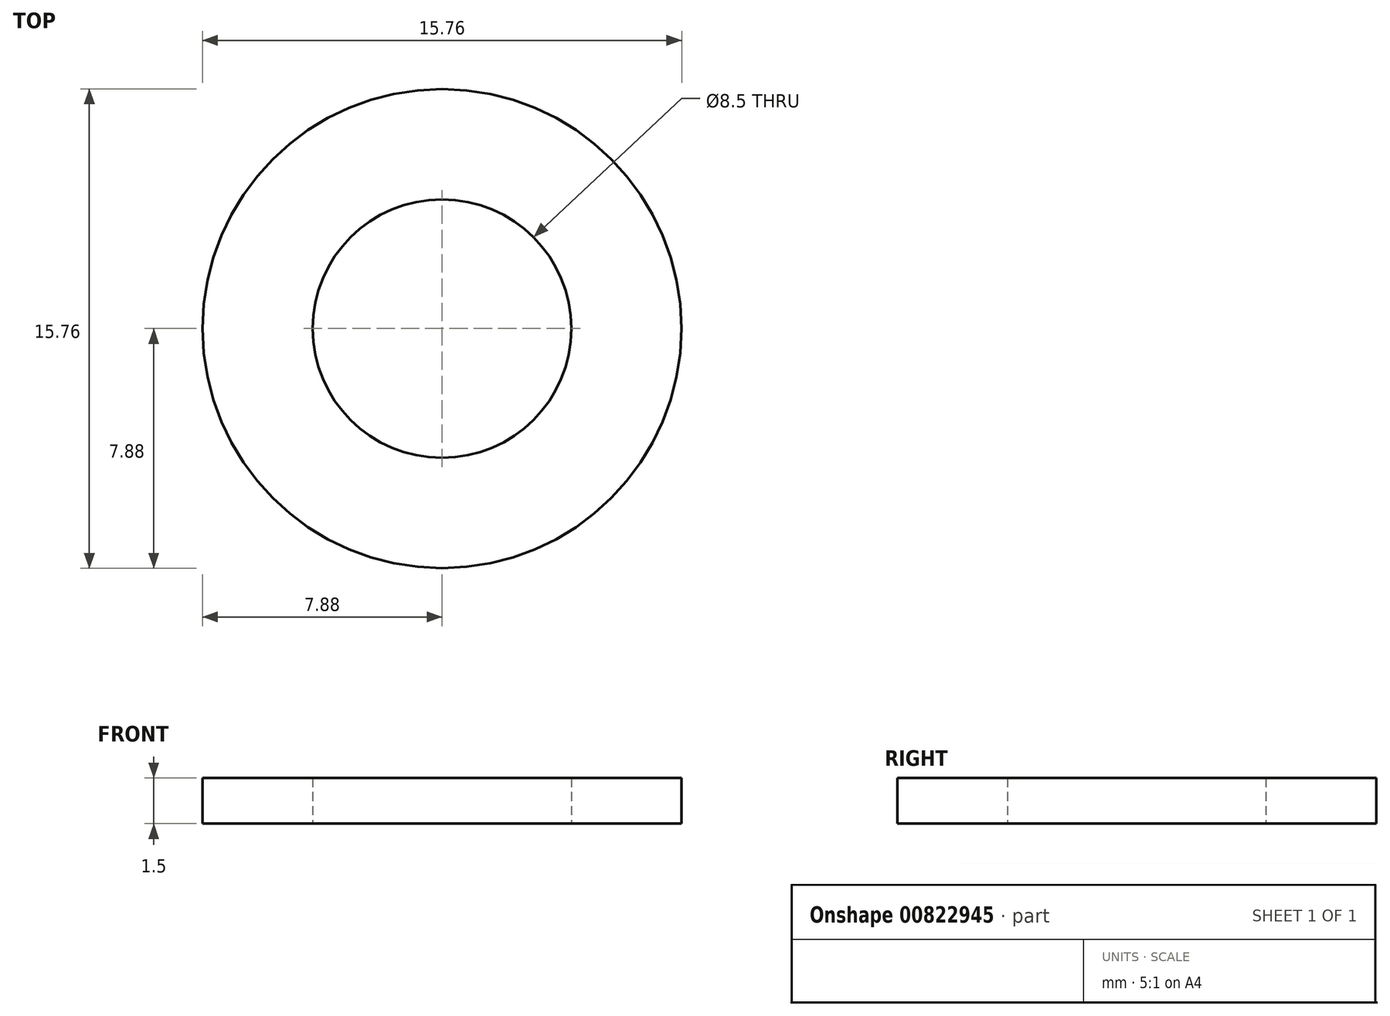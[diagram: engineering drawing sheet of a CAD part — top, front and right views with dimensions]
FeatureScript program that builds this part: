
annotation { "Feature Type Name" : "Feature", "Feature Type Description" : "" }
export const myFeature = defineFeature(function(context is Context, id is Id, definition is map)
    precondition{}
    {
        {
            var Q0;
            Q0=qCreatedBy(makeId("Top.planeOp"),FACE);
            var sketch = newSketch(context, id + "F0", { "sketchPlane" : qUnion([Q0])});
            skCircle(sketch, "E0", {"center": v(0, 0) * mm, "radius": 7.88 * mm});
            skCircle(sketch, "E1", {"center": v(0, 0) * mm, "radius": 4.25 * mm});
            skSolve(sketch);
        }
        {
            var Q0;
            Q0 = qSketchRegion(id + "F0", true);
            extrude(context, id + "F1", {"entities" : qUnion([Q0]), "depth" : 1.5 * mm, "offsetDistance" : 25 * mm});
        }
    });
